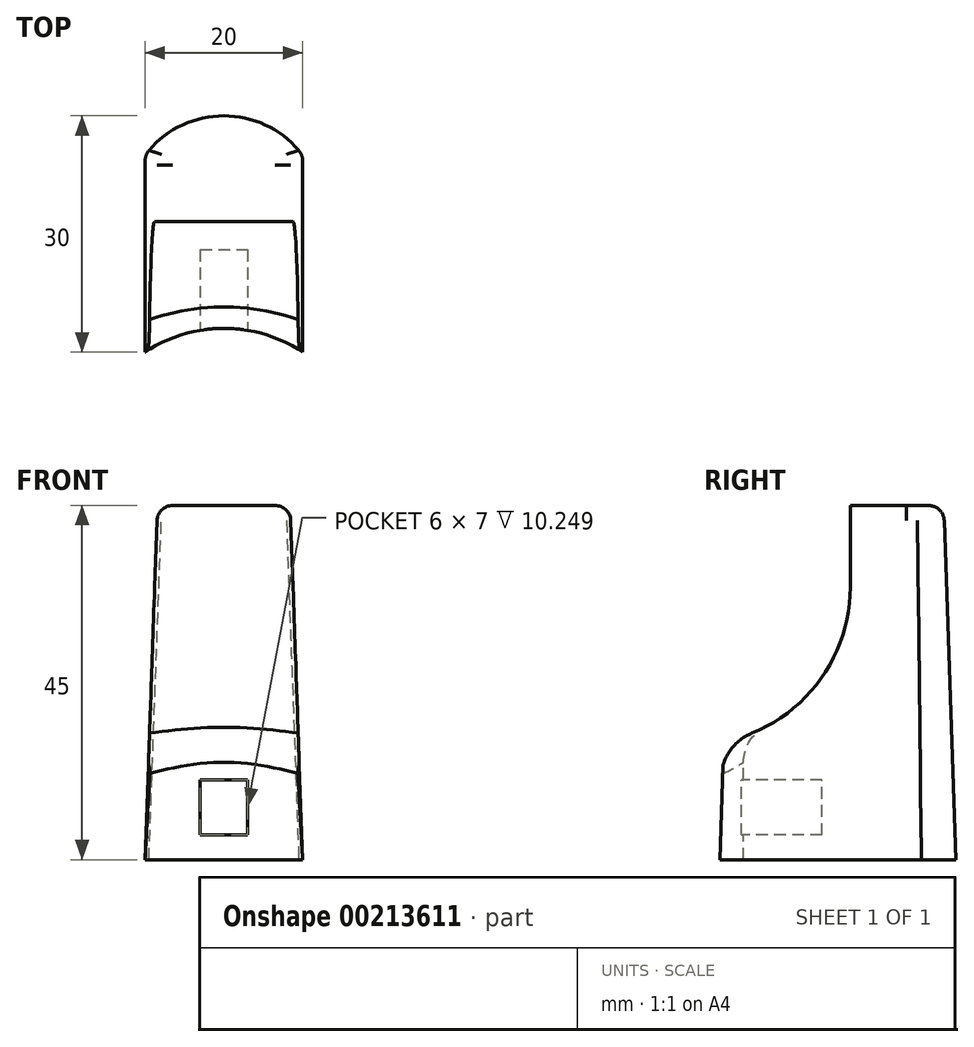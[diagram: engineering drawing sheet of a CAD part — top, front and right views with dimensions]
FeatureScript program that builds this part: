
annotation { "Feature Type Name" : "Feature", "Feature Type Description" : "" }
export const myFeature = defineFeature(function(context is Context, id is Id, definition is map)
    precondition{}
    {
        {
            var Q0;
            Q0=qCreatedBy(makeId("Top.planeOp"),FACE);
            var sketch = newSketch(context, id + "F0", { "sketchPlane" : qUnion([Q0])});
            skLineSegment(sketch, "E0.bottom", {"start": v(-10, -15) * mm, "end": v(10, -15) * mm});
            skLineSegment(sketch, "E0.top", {"start": v(-10, 15) * mm, "end": v(10, 15) * mm});
            skLineSegment(sketch, "E0.left", {"start": v(-10, -15) * mm, "end": v(-10, 15) * mm});
            skLineSegment(sketch, "E0.right", {"start": v(10, -15) * mm, "end": v(10, 15) * mm});
            skPoint(sketch, "E0.middle", {"position": v(0, 0) * mm});
            skLineSegment(sketch, "E1", {"start": v(0, 15) * mm, "end": v(0, 10) * mm, "construction": true});
            skPoint(sketch, "E1.endSnap0", {"position": v(0, 15) * mm});
            skArc(sketch, "E2", {"start": v(10, 10) * mm, "mid": v(0, 15) * mm, "end": v(-10, 10) * mm});
            skSolve(sketch);
        }
        {
            var Q0;
            {var subQ4=sQuery(id+"F0.wireOp",EDGE,"E0.bottom");Q0=makeQuery(id+"F0.imprint","IMPRINT",FACE,{"disambiguationData":[TD([[makeQuery(id+"F0.imprint","IMPRINT",EDGE,{"derivedFrom":subQ4}),1.0]])]});}
            extrude(context, id + "F1", {"entities" : qUnion([Q0]), "depth" : 45 * mm, "hasDraft" : true, "draftAngle" : 2 * degree, "draftPullDirection" : true});
        }
        {
            var Q0;
            Q0=qCreatedBy(makeId("Right.planeOp"),FACE);
            var Q1;
            Q1=makeQuery(id+"F1.opExtrude","CAP_EDGE",EDGE,{"disambiguationData":[OSD([sQuery(id+"F0.wireOp",EDGE,"E0.left")])],"isStart":true});
            cPlane(context, id + "F2", {"entities" : qUnion([Q0, Q1]), "cplaneType" : CPlaneType.LINE_ANGLE, "offset" : 25 * mm, "angle" : 0 * degree, "width" : 150 * mm, "height" : 150 * mm});
        }
        {
            var Q0;
            Q0=qCreatedBy(id+"F2.planeOp",FACE);
            var sketch = newSketch(context, id + "F3", { "sketchPlane" : qUnion([Q0])});
            skLineSegment(sketch, "E3.bottom", {"start": v(13.43, 45) * mm, "end": v(-1.57, 45) * mm});
            skLineSegment(sketch, "E3.top", {"start": v(13.43, 15) * mm, "end": v(-1.57, 15) * mm});
            skLineSegment(sketch, "E3.right", {"start": v(-1.57, 45) * mm, "end": v(-1.57, 15) * mm});
            skLineSegment(sketch, "E4", {"start": v(13.43, 15) * mm, "end": v(14.48, 15) * mm});
            skLineSegment(sketch, "E5", {"start": v(13.43, 45) * mm, "end": v(14.48, 15) * mm});
            skSolve(sketch);
        }
        {
            var Q0;
            Q0=qSketchRegion(id+"F3",true);
            extrude(context, id + "F4", {"entities" : qUnion([Q0]), "operationType" : NewBodyOperationType.REMOVE, "endBound" : BoundingType.THROUGH_ALL, "oppositeDirection" : true, "depth" : 25 * mm});
        }
        {
            var Q0;
            Q0=makeQuery(id+"F4.boolean.opBoolean","COPY",EDGE,{"derivedFrom":makeQuery(id+"F4.opExtrude","SWEPT_EDGE",EDGE,{"disambiguationData":[OSD([sQuery(id+"F3.wireOp",EDGE,"E3.top"),sQuery(id+"F3.wireOp",EDGE,"E3.right")])]})});
            fillet(context, id + "F5", {"entities" : qUnion([Q0]), "radius" : 20 * mm, "tangentPropagation" : true, "allowEdgeOverflow" : false});
        }
        {
            var Q0;
            Q0=qCreatedBy(makeId("Front.planeOp"),FACE);
            var Q1;
            Q1=makeQuery(id+"F1.opExtrude","CAP_EDGE",EDGE,{"disambiguationData":[OSD([sQuery(id+"F0.wireOp",EDGE,"E0.bottom")])],"isStart":true});
            cPlane(context, id + "F6", {"entities" : qUnion([Q0, Q1]), "cplaneType" : CPlaneType.LINE_ANGLE, "offset" : 25 * mm, "angle" : 0 * degree, "width" : 150 * mm, "height" : 150 * mm});
        }
        {
            var Q0;
            Q0=qCreatedBy(id+"F6.planeOp",FACE);
            var sketch = newSketch(context, id + "F7", { "sketchPlane" : qUnion([Q0])});
            skLineSegment(sketch, "E6.bottom", {"start": v(3, 3.13) * mm, "end": v(-3, 3.13) * mm});
            skLineSegment(sketch, "E6.top", {"start": v(3, 10.13) * mm, "end": v(-3, 10.13) * mm});
            skLineSegment(sketch, "E6.left", {"start": v(3, 3.13) * mm, "end": v(3, 10.13) * mm});
            skLineSegment(sketch, "E6.right", {"start": v(-3, 3.13) * mm, "end": v(-3, 10.13) * mm});
            skPoint(sketch, "E6.middle", {"position": v(0, 6.63) * mm});
            skSolve(sketch);
        }
        {
            var Q0;
            Q0=qSketchRegion(id+"F7",true);
            extrude(context, id + "F8", {"entities" : qUnion([Q0]), "operationType" : NewBodyOperationType.REMOVE, "depth" : 13 * mm});
        }
        {
            var Q0;
            Q0=makeQuery(id+"F1.opExtrude","CAP_FACE",FACE,{"disambiguationData":[OSD([sQuery(id+"F0.wireOp",EDGE,"E0.bottom"),sQuery(id+"F0.wireOp",EDGE,"E0.top"),sQuery(id+"F0.wireOp",EDGE,"E0.left"),sQuery(id+"F0.wireOp",EDGE,"E0.right")])],"isStart":false});
            cPlane(context, id + "F9", {"entities" : qUnion([Q0]), "cplaneType" : CPlaneType.OFFSET, "offset" : 0 * mm, "width" : 150 * mm, "height" : 150 * mm});
        }
        {
            var Q0;
            Q0=qCreatedBy(id+"F9.planeOp",FACE);
            var sketch = newSketch(context, id + "F10", { "sketchPlane" : qUnion([Q0])});
            skLineSegment(sketch, "E7", {"start": v(-10, -15) * mm, "end": v(10, -15) * mm});
            skLineSegment(sketch, "E8", {"start": v(0, -15) * mm, "end": v(0, -20) * mm, "construction": true});
            skLineSegment(sketch, "E9", {"start": v(-10, -20) * mm, "end": v(10, -20) * mm});
            skArc(sketch, "E10", {"start": v(10, -20) * mm, "mid": v(0, -15) * mm, "end": v(-10, -20) * mm});
            skLineSegment(sketch, "E11", {"start": v(-10, -15) * mm, "end": v(-10, -20) * mm});
            skLineSegment(sketch, "E12", {"start": v(10, -15) * mm, "end": v(10, -20) * mm});
            skLineSegment(sketch, "E13", {"start": v(0, -15) * mm, "end": v(0, -12) * mm, "construction": true});
            skPoint(sketch, "E13.endSnap0", {"position": v(0, -15) * mm});
            skArc(sketch, "E14", {"start": v(10, -15) * mm, "mid": v(0, -12) * mm, "end": v(-10, -15) * mm});
            skSolve(sketch);
        }
        {
            var Q0;
            {var subQ0=sQuery(id+"F10.wireOp",EDGE,"E11");Q0=makeQuery(id+"F10.imprint","IMPRINT",FACE,{"disambiguationData":[TD([[makeQuery(id+"F10.imprint","IMPRINT",EDGE,{"derivedFrom":subQ0}),1.0]])]});}
            var Q1;
            {var subQ0=sQuery(id+"F10.wireOp",EDGE,"E12");Q1=makeQuery(id+"F10.imprint","IMPRINT",FACE,{"disambiguationData":[TD([[makeQuery(id+"F10.imprint","IMPRINT",EDGE,{"derivedFrom":subQ0}),-1.0]])]});}
            var Q2;
            Q2=makeQuery(id+"F10.imprint","IMPRINT",FACE,{"disambiguationData":[TD([[makeQuery(id+"F10.imprint","IMPRINT",EDGE,{"derivedFrom":sQuery(id+"F10.wireOp",EDGE,"E7")}),1.0]])]});
            extrude(context, id + "F11", {"entities" : qUnion([Q0, Q1, Q2]), "operationType" : NewBodyOperationType.REMOVE, "endBound" : BoundingType.THROUGH_ALL, "oppositeDirection" : true, "depth" : 25 * mm});
        }
        {
            var Q0;
            {var subQ0=sQuery(id+"F10.wireOp",EDGE,"E10");Q0=makeQuery(id+"F11.boolean.opBoolean","INTERSECT",EDGE,{"derivedFrom":[makeQuery(id+"F1.opExtrude","CAP_FACE",FACE,{"disambiguationData":[OSD([sQuery(id+"F0.wireOp",EDGE,"E0.bottom"),sQuery(id+"F0.wireOp",EDGE,"E0.top"),sQuery(id+"F0.wireOp",EDGE,"E0.left"),sQuery(id+"F0.wireOp",EDGE,"E0.right")])],"isStart":true}),makeQuery(id+"F11.opExtrude","SWEPT_FACE",FACE,{"disambiguationData":[OSD([subQ0]),TDD([makeQuery(id+"F10.imprint","IMPRINT",EDGE,{"disambiguationData":[TD([[makeQuery(id+"F10.imprint","INTERSECT",VERTEX,{"derivedFrom":[sQuery(id+"F10.wireOp",EDGE,"E7"),subQ0]}),1.0]])],"derivedFrom":subQ0})])]})]});}
            var Q1;
            Q1=makeQuery(id+"F11.boolean.opBoolean","INTERSECT",EDGE,{"derivedFrom":[makeQuery(id+"F5.opFillet","BLEND_FACE",FACE,{"disambiguationData":[OSD([sQuery(id+"F3.wireOp",EDGE,"E3.top"),sQuery(id+"F3.wireOp",EDGE,"E3.right")])]}),makeQuery(id+"F11.opExtrude","SWEPT_FACE",FACE,{"disambiguationData":[OSD([sQuery(id+"F10.wireOp",EDGE,"E14")])]})]});
            fillet(context, id + "F12", {"entities" : qUnion([Q0, Q1]), "radius" : 5 * mm, "tangentPropagation" : true, "allowEdgeOverflow" : false});
        }
        {
            var Q0;
            Q0=makeQuery(id+"F1.opExtrude","CAP_EDGE",EDGE,{"disambiguationData":[OSD([sQuery(id+"F0.wireOp",EDGE,"E0.top")])],"isStart":false});
            var Q1;
            Q1=makeQuery(id+"F1.opExtrude","CAP_EDGE",EDGE,{"disambiguationData":[OSD([sQuery(id+"F0.wireOp",EDGE,"E0.left")])],"isStart":false});
            var Q2;
            Q2=makeQuery(id+"F1.opExtrude","CAP_EDGE",EDGE,{"disambiguationData":[OSD([sQuery(id+"F0.wireOp",EDGE,"E0.right")])],"isStart":false});
            fillet(context, id + "F13", {"entities" : qUnion([Q0, Q1, Q2]), "radius" : 2 * mm, "tangentPropagation" : true, "allowEdgeOverflow" : false});
        }
        {
            var Q0;
            Q0=makeQuery(id+"F1.opExtrude","CAP_EDGE",EDGE,{"disambiguationData":[OSD([sQuery(id+"F0.wireOp",EDGE,"E2")])],"isStart":false});
            fillet(context, id + "F14", {"entities" : qUnion([Q0]), "radius" : 2 * mm, "tangentPropagation" : true, "allowEdgeOverflow" : false});
        }
    });
